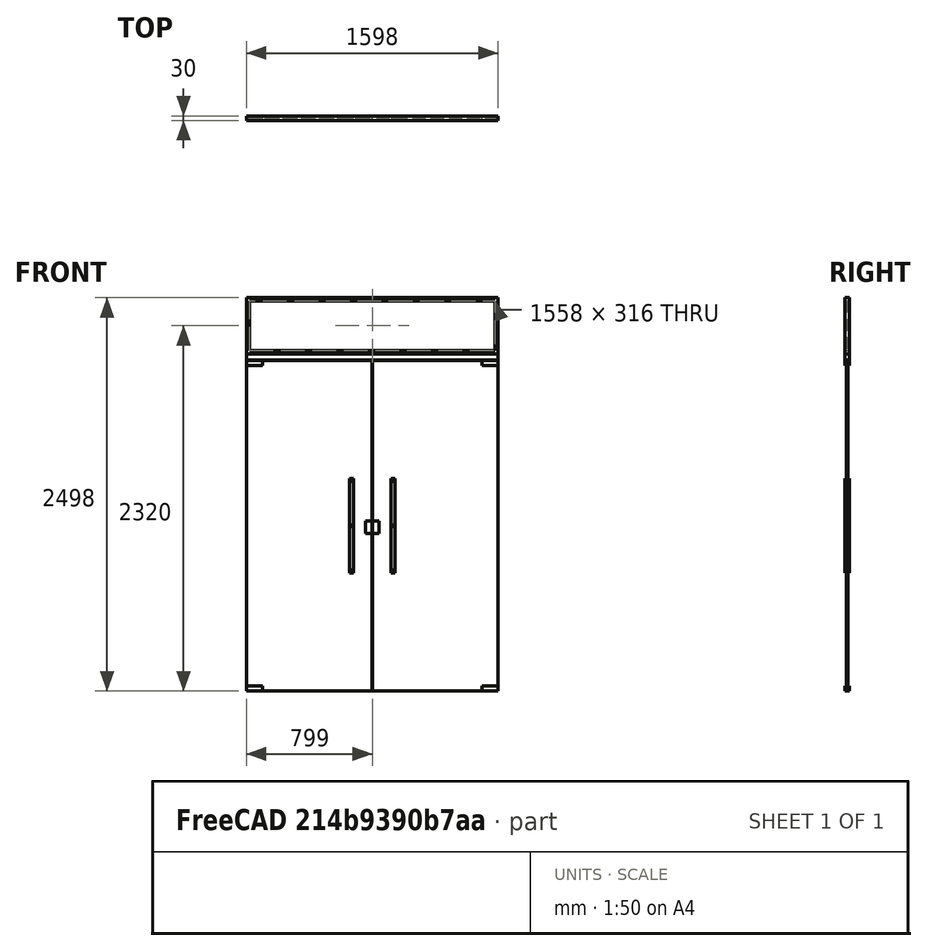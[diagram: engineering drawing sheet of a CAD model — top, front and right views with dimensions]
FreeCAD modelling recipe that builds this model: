
FCSTD DOCUMENT  (FreeCAD 0.16R6704 (Git))
Label: Double glass doors with handles and transom
License: CreativeCommons Attribution
LicenseURL: http://creativecommons.org/licenses/by/4.0/
objects: Sketcher::SketchObject×3, Part::FeaturePython×1, App::DocumentObjectGroup×1
note: 4 computed .brp shape members not serialized (recipe doc carries the construction recipe); baked Part::Feature solids carry a one-line shape summary decoded from their .brp

FEATURE [Sketcher::SketchObject] Sketch130
  Placement = pos=(0,0,0) rot=(1,0,0;1.5708rad)
  sketch-geometry (71):
    g0: LineSegment StartX=0 StartY=0 StartZ=0 EndX=1600 EndY=0 EndZ=0
    g1: LineSegment StartX=1600 StartY=0 StartZ=0 EndX=1600 EndY=2499 EndZ=0
    g2: LineSegment StartX=1600 StartY=2499 StartZ=0 EndX=0 EndY=2499 EndZ=0
    g3: LineSegment StartX=0 StartY=2499 StartZ=0 EndX=0 EndY=0 EndZ=0
    g4: LineSegment StartX=1 StartY=0 StartZ=0 EndX=799.5 EndY=0 EndZ=0
    g5: LineSegment StartX=799.5 StartY=0 StartZ=0 EndX=799.5 EndY=2100 EndZ=0
    g6: LineSegment StartX=799.5 StartY=2100 StartZ=0 EndX=1 EndY=2100 EndZ=0
    g7: LineSegment StartX=1 StartY=2100 StartZ=0 EndX=1 EndY=0 EndZ=0
    g8: LineSegment StartX=2 StartY=2099 StartZ=0 EndX=102 EndY=2099 EndZ=0
    g9: LineSegment StartX=102 StartY=2099 StartZ=0 EndX=102 EndY=2069 EndZ=0
    g10: LineSegment StartX=102 StartY=2069 StartZ=0 EndX=2 EndY=2069 EndZ=0
    g11: LineSegment StartX=2 StartY=2069 StartZ=0 EndX=2 EndY=2099 EndZ=0
    g12: LineSegment StartX=2 StartY=1 StartZ=0 EndX=102 EndY=1 EndZ=0
    g13: LineSegment StartX=102 StartY=1 StartZ=0 EndX=102 EndY=31 EndZ=0
    g14: LineSegment StartX=102 StartY=31 StartZ=0 EndX=2 EndY=31 EndZ=0
    g15: LineSegment StartX=2 StartY=31 StartZ=0 EndX=2 EndY=1 EndZ=0
    g16: LineSegment StartX=758.5 StartY=1080 StartZ=0 EndX=798.5 EndY=1080 EndZ=0
    g17: LineSegment StartX=798.5 StartY=1080 StartZ=0 EndX=798.5 EndY=1000 EndZ=0
    g18: LineSegment StartX=798.5 StartY=1000 StartZ=0 EndX=758.5 EndY=1000 EndZ=0
    g19: LineSegment StartX=758.5 StartY=1000 StartZ=0 EndX=758.5 EndY=1080 EndZ=0
    g20: LineSegment StartX=654.5 StartY=1350 StartZ=0 EndX=679.5 EndY=1350 EndZ=0
    g21: LineSegment StartX=679.5 StartY=1350 StartZ=0 EndX=679.5 EndY=750 EndZ=0
    g22: LineSegment StartX=679.5 StartY=750 StartZ=0 EndX=654.5 EndY=750 EndZ=0
    g23: LineSegment StartX=654.5 StartY=750 StartZ=0 EndX=654.5 EndY=1350 EndZ=0
    g24: LineSegment [constr] StartX=667 StartY=1477.64 StartZ=0 EndX=667 EndY=711 EndZ=0
    g25: Circle CenterX=667 CenterY=1335 CenterZ=0 NormalX=0 NormalY=0 NormalZ=1 Radius=5
    g26: Circle CenterX=667 CenterY=1050 CenterZ=0 NormalX=0 NormalY=0 NormalZ=1 Radius=5
    g27: Circle CenterX=667 CenterY=765 CenterZ=0 NormalX=0 NormalY=0 NormalZ=1 Radius=5
    g28: LineSegment [constr] StartX=712 StartY=1050 StartZ=0 EndX=790 EndY=1050 EndZ=0
    g29: LineSegment [constr] StartX=800 StartY=2724.52 StartZ=0 EndX=800 EndY=-390.353 EndZ=0
    g30: LineSegment StartX=1599 StartY=0.0181393 StartZ=0 EndX=800.5 EndY=0.0181393 EndZ=0
    g31: LineSegment StartX=800.5 StartY=0.0181393 StartZ=0 EndX=800.5 EndY=2100 EndZ=0
    g32: LineSegment StartX=800.5 StartY=2100 StartZ=0 EndX=1599 EndY=2100 EndZ=0
    g33: LineSegment StartX=1599 StartY=2100 StartZ=0 EndX=1599 EndY=0.0181393 EndZ=0
    g34: LineSegment StartX=1598 StartY=2099 StartZ=0 EndX=1498 EndY=2099 EndZ=0
    g35: LineSegment StartX=1498 StartY=2099 StartZ=0 EndX=1498 EndY=2069 EndZ=0
    g36: LineSegment StartX=1498 StartY=2069 StartZ=0 EndX=1598 EndY=2069 EndZ=0
    g37: LineSegment StartX=1598 StartY=2069 StartZ=0 EndX=1598 EndY=2099 EndZ=0
    g38: LineSegment StartX=1598 StartY=1.01814 StartZ=0 EndX=1498 EndY=1.01814 EndZ=0
    g39: LineSegment StartX=1498 StartY=1.01814 StartZ=0 EndX=1498 EndY=31.0181 EndZ=0
    g40: LineSegment StartX=1498 StartY=31.0181 StartZ=0 EndX=1598 EndY=31.0181 EndZ=0
    g41: LineSegment StartX=1598 StartY=31.0181 StartZ=0 EndX=1598 EndY=1.01814 EndZ=0
    g42: LineSegment StartX=841.5 StartY=1080 StartZ=0 EndX=801.5 EndY=1080 EndZ=0
    g43: LineSegment StartX=801.5 StartY=1080 StartZ=0 EndX=801.5 EndY=1000 EndZ=0
    g44: LineSegment StartX=801.5 StartY=1000 StartZ=0 EndX=841.5 EndY=1000 EndZ=0
    g45: LineSegment StartX=841.5 StartY=1000 StartZ=0 EndX=841.5 EndY=1080 EndZ=0
    g46: LineSegment StartX=945.5 StartY=1350 StartZ=0 EndX=920.5 EndY=1350 EndZ=0
    g47: LineSegment StartX=920.5 StartY=1350 StartZ=0 EndX=920.5 EndY=750 EndZ=0
    g48: LineSegment StartX=920.5 StartY=750 StartZ=0 EndX=945.5 EndY=750 EndZ=0
    g49: LineSegment StartX=945.5 StartY=750 StartZ=0 EndX=945.5 EndY=1350 EndZ=0
    g50: LineSegment [constr] StartX=933 StartY=1477.64 StartZ=0 EndX=933 EndY=711 EndZ=0
    g51: Circle CenterX=933 CenterY=1335 CenterZ=0 NormalX=0 NormalY=0 NormalZ=1 Radius=5
    g52: Circle CenterX=933 CenterY=1050 CenterZ=0 NormalX=0 NormalY=0 NormalZ=1 Radius=5
    g53: Circle CenterX=933 CenterY=765 CenterZ=0 NormalX=0 NormalY=0 NormalZ=1 Radius=5
    g54: LineSegment [constr] StartX=1088 StartY=1050 StartZ=0 EndX=1010 EndY=1050 EndZ=0
    g55: LineSegment StartX=-1 StartY=2500 StartZ=0 EndX=1601 EndY=2500 EndZ=0
    g56: LineSegment StartX=1601 StartY=2500 StartZ=0 EndX=1601 EndY=0 EndZ=0
    g57: LineSegment StartX=1601 StartY=0 StartZ=0 EndX=-1 EndY=0 EndZ=0
    g58: LineSegment StartX=-1 StartY=0 StartZ=0 EndX=-1 EndY=2500 EndZ=0
    g59: LineSegment StartX=1 StartY=2498 StartZ=0 EndX=1599 EndY=2498 EndZ=0
    g60: LineSegment StartX=1599 StartY=2498 StartZ=0 EndX=1599 EndY=2142 EndZ=0
    g61: LineSegment StartX=1599 StartY=2142 StartZ=0 EndX=1 EndY=2142 EndZ=0
    g62: LineSegment StartX=1 StartY=2142 StartZ=0 EndX=1 EndY=2498 EndZ=0
    g63: LineSegment StartX=21 StartY=2478 StartZ=0 EndX=1579 EndY=2478 EndZ=0
    g64: LineSegment StartX=1579 StartY=2478 StartZ=0 EndX=1579 EndY=2162 EndZ=0
    g65: LineSegment StartX=1579 StartY=2162 StartZ=0 EndX=21 EndY=2162 EndZ=0
    g66: LineSegment StartX=21 StartY=2162 StartZ=0 EndX=21 EndY=2478 EndZ=0
    g67: LineSegment StartX=1 StartY=2141 StartZ=0 EndX=1599 EndY=2141 EndZ=0
    g68: LineSegment StartX=1599 StartY=2141 StartZ=0 EndX=1599 EndY=2101 EndZ=0
    g69: LineSegment StartX=1599 StartY=2101 StartZ=0 EndX=1 EndY=2101 EndZ=0
    g70: LineSegment StartX=1 StartY=2101 StartZ=0 EndX=1 EndY=2141 EndZ=0
  constraints (203):
    c: Coincident(g0,g1)
    c: Coincident(g1,g2)
    c: Coincident(g2,g3)
    c: Coincident(g3,g0)
    c: Horizontal(g0)
    c: Horizontal(g2)
    c: Vertical(g1)
    c: Vertical(g3)
    c: Coincident(g4,g5)
    c: Coincident(g5,g6)
    c: Coincident(g6,g7)
    c: Coincident(g7,g4)
    c: Horizontal(g4)
    c: Horizontal(g6)
    c: Vertical(g5)
    c: Vertical(g7)
    c: DistanceX(g0) = 1600  'Largura vão'
    c: DistanceX(g2,g6) = 1  'Constraint18'
    c: DistanceY(g0,g4) = 0
    c: Coincident(g0,g-1)
    c: Coincident(g8,g9)
    c: Coincident(g9,g10)
    c: Coincident(g10,g11)
    c: Coincident(g11,g8)
    c: Horizontal(g8)
    c: Horizontal(g10)
    c: Vertical(g9)
    c: Vertical(g11)
    c: Coincident(g12,g13)
    c: Coincident(g13,g14)
    c: Coincident(g14,g15)
    c: Coincident(g15,g12)
    c: Horizontal(g12)
    c: Horizontal(g14)
    c: Vertical(g13)
    c: Vertical(g15)
    c: Coincident(g16,g17)
    c: Coincident(g17,g18)
    c: Coincident(g18,g19)
    c: Coincident(g19,g16)
    c: Horizontal(g16)
    c: Horizontal(g18)
    c: Vertical(g17)
    c: Vertical(g19)
    c: DistanceY(g8,g6) = 1
    c: DistanceX(g6,g8) = 1
    c: DistanceY(g9,g8) = 30
    c: DistanceX(g10,g9) = 100
    c: DistanceX(g4,g12) = 1
    c: DistanceY(g4,g12) = 1
    c: DistanceX(g17,g4) = 1
    c: DistanceY(g18,g16) = 80
    c: DistanceX(g16,g16) = 40
    c: DistanceY(g4,g18) = 1000
    c: Coincident(g20,g21)
    c: Coincident(g21,g22)
    c: Coincident(g22,g23)
    c: Coincident(g23,g20)
    c: Horizontal(g20)
    c: Horizontal(g22)
    c: Vertical(g21)
    c: Vertical(g23)
    c: DistanceX(g20,g20) = 25  'Largura puxador'
    c: DistanceY(g21,g20) = 600  'Altura puxador'
    c: Vertical(g24)  'Constraint69'
    c: Symmetric(g20,g20,g24)  'Constraint67'
    c: PointOnObject(g25,g24)  'Constraint72'
    c: PointOnObject(g26,g24)  'Constraint71'
    c: PointOnObject(g27,g24)
    c: Radius(g27) = 5  'Apoio puxador'
    c: Equal(g27,g26)  'Constraint83'
    c: Equal(g27,g25)  'Constraint82'
    c: DistanceY(g25,g20) = 15  'Constraint73'
    c: DistanceY(g21,g27) = 15
    c: Horizontal(g28)
    c: PointOnObject(g26,g28)
    c: Symmetric(g22,g20,g28)
    c: DistanceY(g4,g21) = 750  'Distância do puxador ao solo'
    c: DistanceX(g21,g4) = 120  'Distância do puxador'
    c: Vertical(g29)
    c: Symmetric(g2,g1,g29)
    c: Coincident(g30,g31)
    c: Coincident(g31,g32)
    c: Coincident(g32,g33)
    c: Coincident(g33,g30)
    c: Horizontal(g30)
    c: Horizontal(g32)
    c: Vertical(g31)
    c: Vertical(g33)
    c: Coincident(g34,g35)
    c: Coincident(g35,g36)
    c: Coincident(g36,g37)
    c: Coincident(g37,g34)
    c: Horizontal(g34)
    c: Horizontal(g36)
    c: Vertical(g35)
    c: Vertical(g37)
    c: Coincident(g38,g39)
    c: Coincident(g39,g40)
    c: Coincident(g40,g41)
    c: Coincident(g41,g38)
    c: Horizontal(g38)
    c: Horizontal(g40)
    c: Vertical(g39)
    c: Vertical(g41)
    c: Coincident(g42,g43)
    c: Coincident(g43,g44)
    c: Coincident(g44,g45)
    c: Coincident(g45,g42)
    c: Horizontal(g42)
    c: Horizontal(g44)
    c: Vertical(g43)
    c: Vertical(g45)
    c: Coincident(g46,g47)
    c: Coincident(g47,g48)
    c: Coincident(g48,g49)
    c: Coincident(g49,g46)
    c: Horizontal(g46)
    c: Horizontal(g48)
    c: Vertical(g47)
    c: Vertical(g49)
    c: Vertical(g50)  'Constraint69'
    c: Symmetric(g46,g46,g50)  'Constraint126'
    c: PointOnObject(g51,g50)  'Constraint72'
    c: PointOnObject(g52,g50)  'Constraint127'
    c: PointOnObject(g53,g50)
    c: Radius(g53) = 5  'Apoio puxador'
    c: Equal(g53,g52)  'Constraint83'
    c: Equal(g53,g51)  'Constraint82'
    c: Horizontal(g54)
    c: PointOnObject(g52,g54)
    c: Symmetric(g48,g46,g54)
    c: Coincident(g55,g56)
    c: Coincident(g56,g57)
    c: Coincident(g57,g58)
    c: Coincident(g58,g55)
    c: Horizontal(g55)
    c: Horizontal(g57)
    c: Vertical(g56)
    c: Vertical(g58)
    c: DistanceX(g55,g2) = 1
    c: DistanceY(g2,g55) = 1
    c: DistanceX(g1,g55) = 1
    c: DistanceY(g57,g-1) = 0
    c: DistanceY(g-1,g6) = 2100  'Altura portas'
    c: Coincident(g59,g60)
    c: Coincident(g60,g61)
    c: Coincident(g61,g62)
    c: Coincident(g62,g59)
    c: Horizontal(g59)
    c: Horizontal(g61)
    c: Vertical(g60)
    c: Vertical(g62)
    c: Coincident(g63,g64)
    c: Coincident(g64,g65)
    c: Coincident(g65,g66)
    c: Coincident(g66,g63)
    c: Horizontal(g63)
    c: Horizontal(g65)
    c: Vertical(g64)
    c: Vertical(g66)
    c: Coincident(g67,g68)
    c: Coincident(g68,g69)
    c: Coincident(g69,g70)
    c: Coincident(g70,g67)
    c: Horizontal(g67)
    c: Horizontal(g69)
    c: Vertical(g68)
    c: Vertical(g70)
    c: DistanceX(g67,g61) = 0
    c: DistanceY(g67,g61) = 1
    c: DistanceY(g61,g65) = 20  'Altura perfil bandeira 1'
    c: DistanceX(g61,g65) = 20  'Largura perfil bandeira 1'
    c: DistanceY(g63,g59) = 20  'Altura perfil bandeira 2'
    c: DistanceX(g63,g59) = 20  'Largura perfil bandeira'
    c: DistanceX(g60,g67) = 0
    c: DistanceX(g30,g0) = 1
    c: DistanceX(g68,g32) = 0
    c: DistanceX(g6,g69) = 0
    c: DistanceY(g6,g69) = 1
    c: DistanceY(g69,g67) = 40  'Altura perfil bandeira'
    c: DistanceY(g59,g2) = 1
    c: DistanceY(g6,g55) = 400  'Altura bandeira'
    c: Symmetric(g55,g55,g29)
    c: DistanceX(g34,g32) = 1
    c: DistanceY(g34,g32) = 1
    c: DistanceY(g30,g38) = 1
    c: DistanceX(g38,g30) = 1
    c: DistanceY(g31,g5) = 0
    c: Symmetric(g5,g31,g29)
    c: Symmetric(g24,g50,g29)
    c: Equal(g9,g35)
    c: Equal(g35,g39)
    c: Equal(g39,g13)
    c: Equal(g10,g36)
    c: Equal(g36,g40)
    c: Equal(g40,g14)
    c: DistanceX(g5,g31) = 1
    c: Equal(g20,g46)
    c: Symmetric(g16,g42,g29)
    c: DistanceX(g16,g42) = 3
    c: Equal(g16,g42)
    c: Equal(g19,g45)
FEATURE [Part::FeaturePython] Window093  label="Double glass doors with handles and transom 001"  # WARN: FeaturePython — macro-defined, semantics opaque (R4)
  Base = -> Sketch130
  Height = 2100
  HoleDepth = 0
  MoveWithHost = true
  Normal = (0,1,0)
  Preset = 6
  Role = 1
  Width = 900
  WindowParts = PORTA 1 | Glass panel | Wire1 | 10.0 | 10.0 | APOIO SUPERIOR PORTA 1 | Frame | Wire2 | 30.0 | 0.0 | APOIO INFERIOR PORTA 1 | Frame | Wire3 | 30.0 | 0.0 | TRANCA 1 | Frame | Wire4 | 30.0 | 0.0 | PUXADOR 1A | Frame | Wire5 | 10.0 | 0.0 | PUXADOR 2A | Frame | Wire13 | 10.0 | 0.0 | APOIO SUPERIOR PUXADOR 1 | Frame | Wire6 | 30.0 | 0.0 | APOIO CENTRAL PUXADOR 1 | Frame | Wire7 | 30.0 | 0.0 | APOIO INFERIOR PUXADOR 1 | Frame | Wire8 | 30.0 | 0.0 | PORTA 2 | Glass panel | Wire9 | 10.0 | 10.0 | APOIO SUPERIOR PORTA 2 | Frame | Wire10 | 30.0 | 0.0 | APOIO INFERIOR PORTA 2 | Frame | Wire11 | 30.0 | 0.0 | TRANCA 2 | Frame | Wire12 | 30.0 | 0.0 | APOIO SUPERIOR PUXADOR 2 | Frame | Wire14 | 30.0 | 0.0 | APOIO CENTRAL PUXADOR 2 | Frame | Wire15 | 30.0 | 0.0 | APOIO INFERIOR PUXADOR 2 | Frame | Wire16 | 30.0 | 0.0 | PUXADOR 2B | Frame | Wire13 | 10.0 | 20.0 | PERFIL BASE BANDEIRA | Frame | Wire20 | 30.0 | 0.0 | PERFIL BANDEIRA | Frame | Wire19,Wire18 | 30.0 | 0.0 | VIDRO BANDEIRA | Glass panel | Wire19 | 10.0 | 5.0 | PUXADOR 1B | Frame | Wire5 | 10.0 | 20.0
FEATURE [Sketcher::SketchObject] Sketch131  label="Opening indication "
  ExternalGeometry = -> [Window093]
  Placement = pos=(0,10,0) rot=(1,0,0;1.5708rad)
  Support = -> Window093 [Face5]
  sketch-geometry (6):
    g0: LineSegment [constr] StartX=-578.323 StartY=1041.81 StartZ=0 EndX=1784.68 EndY=1041.81 EndZ=0
    g1: LineSegment [constr] StartX=60 StartY=2317.2 StartZ=0 EndX=60 EndY=-99.6345 EndZ=0
    g2: LineSegment StartX=1 StartY=1041.81 StartZ=0 EndX=60 EndY=2100 EndZ=0
    g3: LineSegment StartX=60 StartY=2100 StartZ=0 EndX=799.5 EndY=1041.81 EndZ=0
    g4: LineSegment StartX=799.5 StartY=1041.81 StartZ=0 EndX=60 EndY=0 EndZ=0
    g5: LineSegment StartX=60 StartY=0 StartZ=0 EndX=1 EndY=1041.81 EndZ=0
  constraints (16):
    c: Horizontal(g0)
    c: DistanceY(g-1,g0) = 1041.81  'Altura tranca'
    c: Vertical(g1)
    c: PointOnObject(g2,g0)
    c: Coincident(g2,g3)
    c: PointOnObject(g3,g-5)
    c: Coincident(g3,g4)
    c: PointOnObject(g4,g-6)
    c: Coincident(g4,g5)
    c: Coincident(g5,g2)
    c: PointOnObject(g2,g-4)
    c: PointOnObject(g2,g-3)
    c: PointOnObject(g2,g1)
    c: PointOnObject(g4,g1)
    c: PointOnObject(g3,g0)
    c: DistanceX(g-1,g1) = 60  'Eixo porta'
FEATURE [Sketcher::SketchObject] Sketch132  label="Opening indication 001"
  ExternalGeometry = -> [Window093]
  Placement = pos=(0,10,0) rot=(1,0,0;1.5708rad)
  Support = -> Window093 [Face50]
  sketch-geometry (6):
    g0: LineSegment [constr] StartX=-496.649 StartY=1041.19 StartZ=0 EndX=2033.7 EndY=1041.19 EndZ=0
    g1: LineSegment [constr] StartX=1539 StartY=2387.2 StartZ=0 EndX=1539 EndY=-146 EndZ=0
    g2: LineSegment StartX=799.5 StartY=1041.19 StartZ=0 EndX=1539 EndY=0.0181393 EndZ=0
    g3: LineSegment StartX=1539 StartY=0.0181393 StartZ=0 EndX=1599 EndY=1041.19 EndZ=0
    g4: LineSegment StartX=1599 StartY=1041.19 StartZ=0 EndX=1539 EndY=2100 EndZ=0
    g5: LineSegment StartX=1539 StartY=2100 StartZ=0 EndX=799.5 EndY=1041.19 EndZ=0
  constraints (16):
    c: Horizontal(g0)
    c: DistanceY(g-1,g0) = 1041.19  'Altura da tranca'
    c: Vertical(g1)
    c: DistanceX(g1,g-6) = 60  'Eixo porta'
    c: PointOnObject(g2,g-4)
    c: PointOnObject(g2,g-6)
    c: Coincident(g2,g3)
    c: PointOnObject(g3,g-5)
    c: Coincident(g3,g4)
    c: PointOnObject(g4,g-3)
    c: Coincident(g4,g5)
    c: Coincident(g5,g2)
    c: PointOnObject(g2,g0)
    c: PointOnObject(g3,g0)
    c: PointOnObject(g2,g1)
    c: PointOnObject(g4,g1)
FEATURE [App::DocumentObjectGroup] Grupo100  label="Double glass doors with handles and transom "
  Group = -> [Window093,Sketch131,Sketch132]
